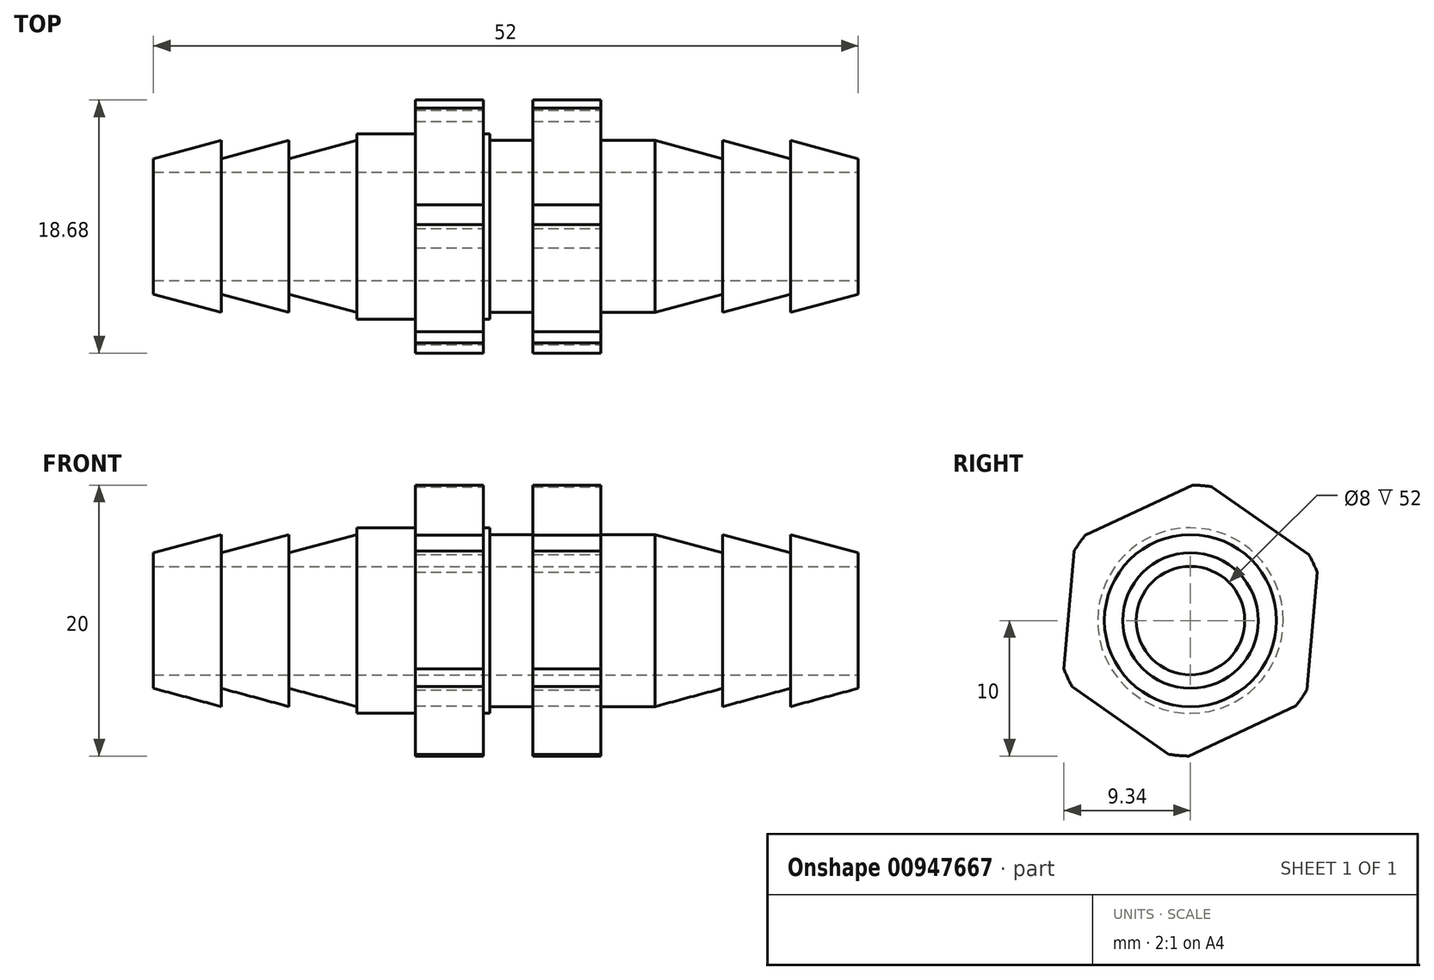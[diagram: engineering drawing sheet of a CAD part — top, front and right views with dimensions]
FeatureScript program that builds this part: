
annotation { "Feature Type Name" : "Feature", "Feature Type Description" : "" }
export const myFeature = defineFeature(function(context is Context, id is Id, definition is map)
    precondition{}
    {
        {
            var Q0;
            Q0=qCreatedBy(makeId("Front.planeOp"),FACE);
            var sketch = newSketch(context, id + "F0", { "sketchPlane" : qUnion([Q0])});
            skLineSegment(sketch, "E0", {"start": v(0, 0) * mm, "end": v(-52, 0) * mm});
            skLineSegment(sketch, "E1", {"start": v(-52, 4) * mm, "end": v(-52, 5) * mm});
            skLineSegment(sketch, "E2", {"start": v(-19, 6.35) * mm, "end": v(-19, 10) * mm});
            skLineSegment(sketch, "E3", {"start": v(-19, 10) * mm, "end": v(-24, 10) * mm});
            skLineSegment(sketch, "E4", {"start": v(-19, 6.35) * mm, "end": v(-15, 6.35) * mm});
            skLineSegment(sketch, "E5", {"start": v(0, 4) * mm, "end": v(0, 6.35) * mm});
            skLineSegment(sketch, "E6", {"start": v(-24, 10) * mm, "end": v(-24, 6.35) * mm});
            skLineSegment(sketch, "E7", {"start": v(-24, 6.35) * mm, "end": v(-27.18, 6.35) * mm});
            skLineSegment(sketch, "E8", {"start": v(-27.18, 6.35) * mm, "end": v(-27.18, 6.85) * mm});
            skLineSegment(sketch, "E9", {"start": v(-27.18, 6.85) * mm, "end": v(-27.67, 6.85) * mm});
            skLineSegment(sketch, "E10", {"start": v(-27.67, 6.85) * mm, "end": v(-27.67, 10) * mm});
            skLineSegment(sketch, "E11", {"start": v(-27.67, 10) * mm, "end": v(-32.67, 10) * mm});
            skLineSegment(sketch, "E12", {"start": v(-32.67, 10) * mm, "end": v(-32.67, 6.85) * mm});
            skLineSegment(sketch, "E13", {"start": v(-32.67, 6.85) * mm, "end": v(-37, 6.85) * mm});
            skLineSegment(sketch, "E14", {"start": v(-37, 6.85) * mm, "end": v(-37, 6.35) * mm});
            skPoint(sketch, "E15.orphan", {"position": v(-52, 5) * mm});
            skLineSegment(sketch, "E16", {"start": v(-52, 4) * mm, "end": v(0, 4) * mm});
            skPoint(sketch, "E16.endSnap0", {"position": v(0, 3.17) * mm});
            skLineSegment(sketch, "E17", {"start": v(-15, 6.35) * mm, "end": v(-10, 5) * mm});
            skLineSegment(sketch, "E18", {"start": v(-10, 5) * mm, "end": v(-10, 6.35) * mm});
            skLineSegment(sketch, "E19", {"start": v(-10, 6.35) * mm, "end": v(-5, 5) * mm});
            skLineSegment(sketch, "E20", {"start": v(-5, 5) * mm, "end": v(-5, 6.35) * mm});
            skLineSegment(sketch, "E21", {"start": v(-5, 6.35) * mm, "end": v(0, 5) * mm});
            skLineSegment(sketch, "E22", {"start": v(-37, 6.35) * mm, "end": v(-42, 5) * mm});
            skLineSegment(sketch, "E23", {"start": v(-42, 5) * mm, "end": v(-42, 6.35) * mm});
            skLineSegment(sketch, "E24", {"start": v(-42, 6.35) * mm, "end": v(-47, 5) * mm});
            skLineSegment(sketch, "E25", {"start": v(-47, 5) * mm, "end": v(-47, 6.35) * mm});
            skLineSegment(sketch, "E26", {"start": v(-47, 6.35) * mm, "end": v(-52, 5) * mm});
            skPoint(sketch, "E27.orphan", {"position": v(-52, 6.35) * mm});
            skSolve(sketch);
        }
        {
            var Q0;
            Q0=qSketchRegion(id+"F0",true);
            var Q1;
            Q1=sQuery(id+"F0.wireOp",EDGE,"E0");
            revolve(context, id + "F1", {"surfaceOperationType" : NewSurfaceOperationType.NEW, "entities" : qUnion([Q0]), "axis" : qUnion([Q1]), "revolveType" : RevolveType.FULL});
        }
        {
            var Q0;
            Q0=qCreatedBy(makeId("Right.planeOp"),FACE);
            var sketch = newSketch(context, id + "F2", { "sketchPlane" : qUnion([Q0])});
            skCircle(sketch, "E28.cCircle", {"center": v(0, 0) * mm, "radius": 9 * mm, "construction": true});
            skLineSegment(sketch, "E28.0", {"start": v(9.42, 4.4) * mm, "end": v(8.52, -5.96) * mm});
            skLineSegment(sketch, "E28.1", {"start": v(8.52, -5.96) * mm, "end": v(-0.9, -10.35) * mm});
            skLineSegment(sketch, "E28.2", {"start": v(-0.9, -10.35) * mm, "end": v(-9.42, -4.4) * mm});
            skLineSegment(sketch, "E28.3", {"start": v(-9.42, -4.4) * mm, "end": v(-8.52, 5.96) * mm});
            skLineSegment(sketch, "E28.4", {"start": v(-8.52, 5.96) * mm, "end": v(0.9, 10.35) * mm});
            skLineSegment(sketch, "E28.5", {"start": v(0.9, 10.35) * mm, "end": v(9.42, 4.4) * mm});
            skPoint(sketch, "E28.0.midPoint", {"position": v(8.97, -0.78) * mm});
            skCircle(sketch, "E29", {"center": v(0, 0) * mm, "radius": 21.39 * mm});
            skSolve(sketch);
        }
        {
            var Q0;
            Q0=qSketchRegion(id+"F2",true);
            extrude(context, id + "F3", {"entities" : qUnion([Q0]), "operationType" : NewBodyOperationType.REMOVE, "oppositeDirection" : true, "depth" : 50.9 * mm, "offsetDistance" : 25 * mm});
        }
    });
